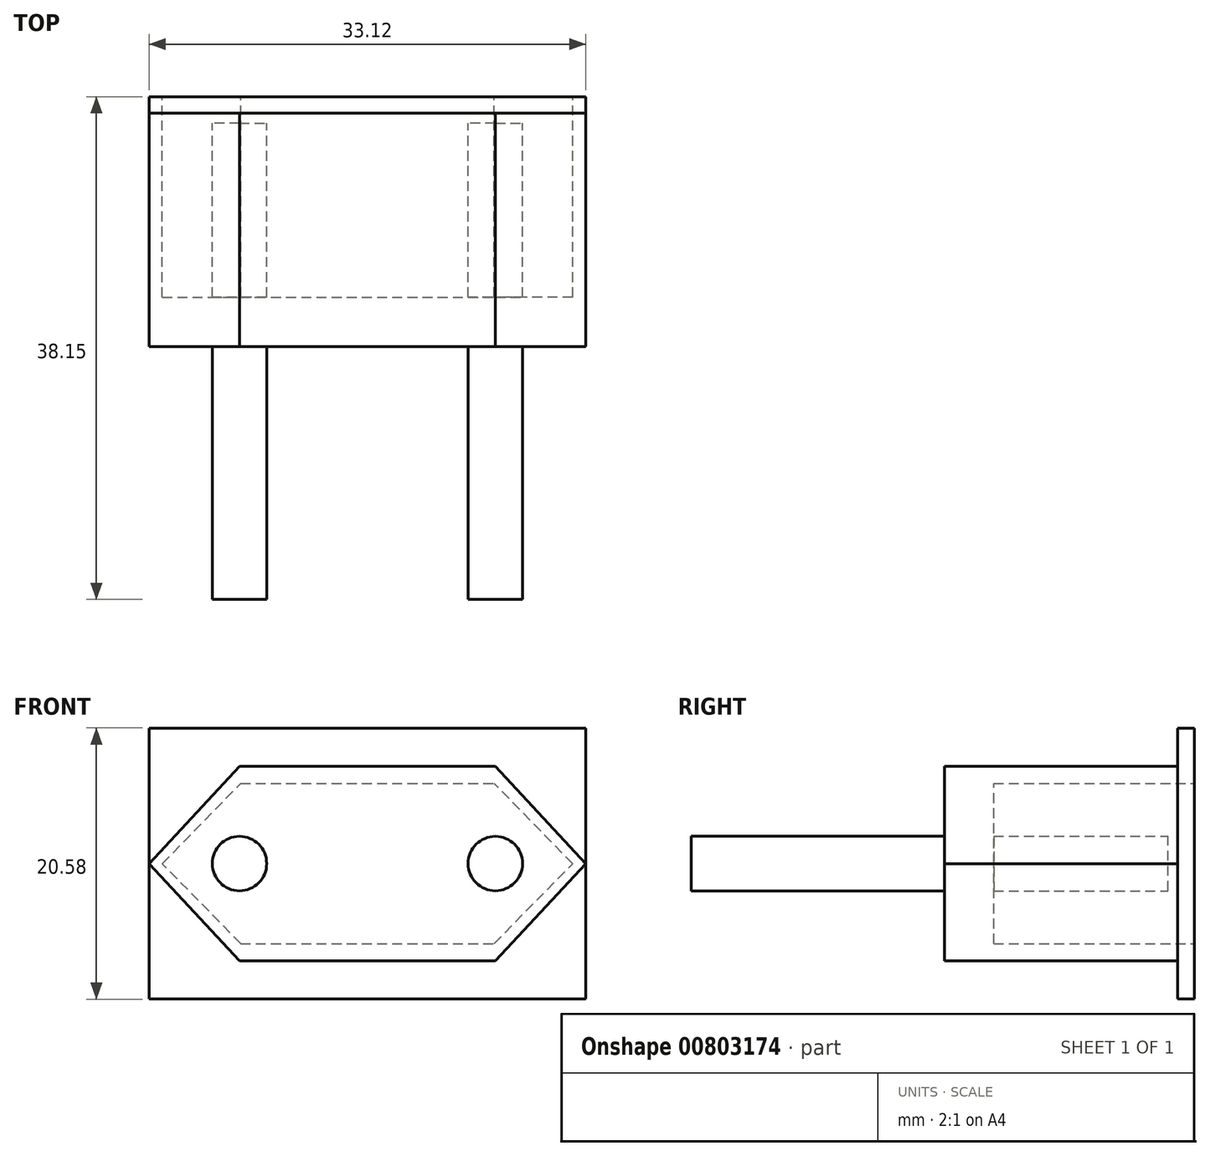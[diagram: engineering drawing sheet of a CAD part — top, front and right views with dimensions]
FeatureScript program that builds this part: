
annotation { "Feature Type Name" : "Feature", "Feature Type Description" : "" }
export const myFeature = defineFeature(function(context is Context, id is Id, definition is map)
    precondition{}
    {
        {
            var Q0;
            Q0=qCreatedBy(makeId("Front.planeOp"),FACE);
            var sketch = newSketch(context, id + "F0", { "sketchPlane" : qUnion([Q0])});
            skLineSegment(sketch, "E0.bottom", {"start": v(16.56, 10.29) * mm, "end": v(-16.56, 10.29) * mm});
            skLineSegment(sketch, "E0.top", {"start": v(16.56, -10.29) * mm, "end": v(-16.56, -10.29) * mm});
            skLineSegment(sketch, "E0.left", {"start": v(16.56, 10.29) * mm, "end": v(16.56, -10.29) * mm});
            skLineSegment(sketch, "E0.right", {"start": v(-16.56, 10.29) * mm, "end": v(-16.56, -10.29) * mm});
            skPoint(sketch, "E0.middle", {"position": v(0, 0) * mm});
            skSolve(sketch);
        }
        {
            var Q0;
            Q0 = qSketchRegion(id + "F0", true);
            extrude(context, id + "F1", {"entities" : qUnion([Q0]), "endBound" : BoundingType.SYMMETRIC, "depth" : 1.26 * mm, "offsetDistance" : 25 * mm});
        }
        {
            var Q0;
            Q0=makeQuery(id+"F1.opExtrude","CAP_FACE",FACE,{"disambiguationData":[OSD([sQuery(id+"F0.wireOp",EDGE,"E0.bottom"),sQuery(id+"F0.wireOp",EDGE,"E0.top"),sQuery(id+"F0.wireOp",EDGE,"E0.left"),sQuery(id+"F0.wireOp",EDGE,"E0.right")])],"isStart":false});
            var sketch = newSketch(context, id + "F2", { "sketchPlane" : qUnion([Q0])});
            skLineSegment(sketch, "E1.bottom", {"start": v(9.7, 7.38) * mm, "end": v(-9.7, 7.38) * mm});
            skLineSegment(sketch, "E1.top", {"start": v(9.7, -7.38) * mm, "end": v(-9.7, -7.38) * mm});
            skPoint(sketch, "E1.middle", {"position": v(0, 0) * mm});
            skLineSegment(sketch, "E2", {"start": v(-9.7, 7.38) * mm, "end": v(-16.56, 0) * mm});
            skLineSegment(sketch, "E3", {"start": v(-16.56, 0) * mm, "end": v(-9.7, -7.38) * mm});
            skLineSegment(sketch, "E4", {"start": v(9.7, 7.38) * mm, "end": v(16.56, 0) * mm});
            skLineSegment(sketch, "E5", {"start": v(16.56, 0) * mm, "end": v(9.7, -7.38) * mm});
            skSolve(sketch);
        }
        {
            var Q0;
            Q0 = qSketchRegion(id + "F2", true);
            extrude(context, id + "F3", {"entities" : qUnion([Q0]), "operationType" : NewBodyOperationType.ADD, "depth" : 17.7 * mm, "offsetDistance" : 25 * mm});
        }
        {
            var Q0;
            Q0=makeQuery(id+"F1.opExtrude","CAP_FACE",FACE,{"disambiguationData":[OSD([sQuery(id+"F0.wireOp",EDGE,"E0.bottom"),sQuery(id+"F0.wireOp",EDGE,"E0.top"),sQuery(id+"F0.wireOp",EDGE,"E0.left"),sQuery(id+"F0.wireOp",EDGE,"E0.right")])],"isStart":true});
            var sketch = newSketch(context, id + "F4", { "sketchPlane" : qUnion([Q0])});
            skPoint(sketch, "E6.middle", {"position": v(0, 0) * mm});
            skLineSegment(sketch, "E7.bottom", {"start": v(9.62, 6.08) * mm, "end": v(-9.61, 6.08) * mm});
            skLineSegment(sketch, "E7.top", {"start": v(9.61, -6.08) * mm, "end": v(-9.62, -6.08) * mm});
            skLineSegment(sketch, "E7.left", {"start": v(9.62, 6.08) * mm, "end": v(9.62, -6.08) * mm});
            skLineSegment(sketch, "E7.right", {"start": v(-9.62, 6.08) * mm, "end": v(-9.62, -6.08) * mm});
            skLineSegment(sketch, "E8", {"start": v(-16.56, 0) * mm, "end": v(-15.56, 0) * mm});
            skLineSegment(sketch, "E9", {"start": v(-15.56, 0) * mm, "end": v(-9.61, 6.08) * mm});
            skLineSegment(sketch, "E10", {"start": v(-9.62, -6.08) * mm, "end": v(-15.56, 0) * mm});
            skLineSegment(sketch, "E11", {"start": v(16.56, 0) * mm, "end": v(15.56, 0) * mm});
            skLineSegment(sketch, "E12", {"start": v(15.56, 0) * mm, "end": v(9.62, 6.08) * mm});
            skLineSegment(sketch, "E13", {"start": v(9.61, -6.08) * mm, "end": v(15.56, 0) * mm});
            skSolve(sketch);
        }
        {
            var Q0;
            Q0 = qSketchRegion(id + "F4", true);
            extrude(context, id + "F5", {"entities" : qUnion([Q0]), "operationType" : NewBodyOperationType.REMOVE, "oppositeDirection" : true, "depth" : 15.21 * mm, "hasOffset" : true, "offsetDistance" : 0.86 * mm});
        }
        {
            var Q0;
            Q0=makeQuery(id+"F3.opExtrude","CAP_FACE",FACE,{"disambiguationData":[OSD([sQuery(id+"F2.wireOp",EDGE,"E1.bottom"),sQuery(id+"F2.wireOp",EDGE,"E1.top"),sQuery(id+"F2.wireOp",EDGE,"E2"),sQuery(id+"F2.wireOp",EDGE,"E3"),sQuery(id+"F2.wireOp",EDGE,"E4"),sQuery(id+"F2.wireOp",EDGE,"E5")])],"isStart":false});
            var sketch = newSketch(context, id + "F6", { "sketchPlane" : qUnion([Q0])});
            skCircle(sketch, "E14", {"center": v(-9.7, 0) * mm, "radius": 2.06 * mm});
            skLineSegment(sketch, "E15", {"start": v(0, 0) * mm, "end": v(0, 7.38) * mm});
            skCircle(sketch, "E16.MirrorC", {"center": v(9.7, 0) * mm, "radius": 2.06 * mm});
            skSolve(sketch);
        }
        {
            var Q0;
            Q0 = qSketchRegion(id + "F6", true);
            var Q1;
            Q1=makeQuery(id+"F1.opExtrude","CAP_FACE",FACE,{"disambiguationData":[OSD([sQuery(id+"F0.wireOp",EDGE,"E0.bottom"),sQuery(id+"F0.wireOp",EDGE,"E0.top"),sQuery(id+"F0.wireOp",EDGE,"E0.left"),sQuery(id+"F0.wireOp",EDGE,"E0.right")])],"isStart":true});
            extrude(context, id + "F7", {"entities" : qUnion([Q0]), "operationType" : NewBodyOperationType.ADD, "depth" : 19.2 * mm, "offsetDistance" : 25 * mm, "hasSecondDirection" : true, "secondDirectionBound" : SecondDirectionBoundingType.UP_TO_SURFACE, "secondDirectionOppositeDirection" : true, "secondDirectionDepth" : 25 * mm, "secondDirectionBoundEntityFace" : qUnion([Q1]), "hasSecondDirectionOffset" : true, "secondDirectionOffsetDistance" : 2 * mm});
        }
    });
